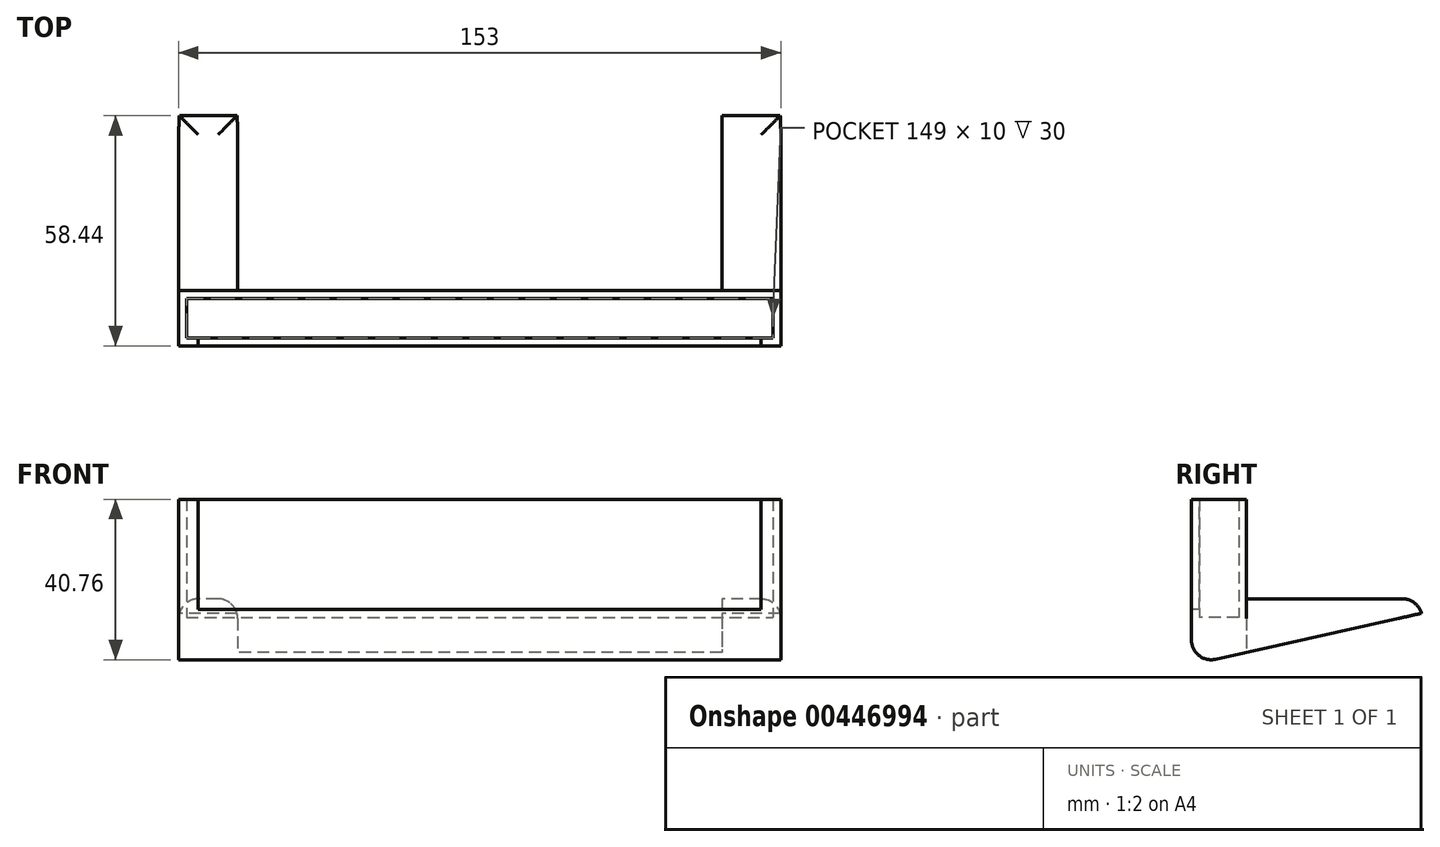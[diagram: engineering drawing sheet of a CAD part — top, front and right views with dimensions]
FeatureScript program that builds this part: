
annotation { "Feature Type Name" : "Feature", "Feature Type Description" : "" }
export const myFeature = defineFeature(function(context is Context, id is Id, definition is map)
    precondition{}
    {
        {
            var Q0;
            Q0=qCreatedBy(makeId("Top.planeOp"),FACE);
            var sketch = newSketch(context, id + "F0", { "sketchPlane" : qUnion([Q0])});
            skLineSegment(sketch, "E0.bottom", {"start": v(-58.19, 12) * mm, "end": v(90.81, 12) * mm});
            skLineSegment(sketch, "E0.top", {"start": v(-58.19, 2) * mm, "end": v(90.81, 2) * mm});
            skLineSegment(sketch, "E0.left", {"start": v(-58.19, 12) * mm, "end": v(-58.19, 2) * mm});
            skLineSegment(sketch, "E0.right", {"start": v(90.81, 12) * mm, "end": v(90.81, 2) * mm});
            skLineSegment(sketch, "E1.bottom", {"start": v(-60.19, 14) * mm, "end": v(92.81, 14) * mm});
            skLineSegment(sketch, "E1.top", {"start": v(-60.19, 0) * mm, "end": v(92.81, 0) * mm});
            skLineSegment(sketch, "E1.left", {"start": v(-60.19, 14) * mm, "end": v(-60.19, 0) * mm});
            skLineSegment(sketch, "E1.right", {"start": v(92.81, 14) * mm, "end": v(92.81, 0) * mm});
            skSolve(sketch);
        }
        {
            var Q0;
            Q0=makeQuery(id+"F0.imprint","IMPRINT",FACE,{"disambiguationData":[TD([[makeQuery(id+"F0.imprint","IMPRINT",EDGE,{"derivedFrom":sQuery(id+"F0.wireOp",EDGE,"E0.bottom")}),1.0]])]});
            extrude(context, id + "F1", {"entities" : qUnion([Q0]), "depth" : 32 * mm});
        }
        {
            var Q0;
            Q0=makeQuery(id+"F0.imprint","IMPRINT",FACE,{"disambiguationData":[TD([[makeQuery(id+"F0.imprint","IMPRINT",EDGE,{"derivedFrom":sQuery(id+"F0.wireOp",EDGE,"E0.bottom")}),-1.0]])]});
            extrude(context, id + "F2", {"entities" : qUnion([Q0]), "operationType" : NewBodyOperationType.ADD, "depth" : 2 * mm});
        }
        {
            var Q0;
            Q0=makeQuery(id+"F1.opExtrude","SWEPT_FACE",FACE,{"disambiguationData":[OSD([sQuery(id+"F0.wireOp",EDGE,"E1.top")])]});
            var sketch = newSketch(context, id + "F3", { "sketchPlane" : qUnion([Q0])});
            skLineSegment(sketch, "E2.bottom", {"start": v(-55.19, 32) * mm, "end": v(87.81, 32) * mm});
            skLineSegment(sketch, "E2.top", {"start": v(-55.19, 4) * mm, "end": v(87.81, 4) * mm});
            skLineSegment(sketch, "E2.left", {"start": v(-55.19, 32) * mm, "end": v(-55.19, 4) * mm});
            skLineSegment(sketch, "E2.right", {"start": v(87.81, 32) * mm, "end": v(87.81, 4) * mm});
            skSolve(sketch);
        }
        {
            var Q0;
            Q0=makeQuery(id+"F3.imprint","IMPRINT",FACE,{"disambiguationData":[TD([[makeQuery(id+"F3.imprint","IMPRINT",EDGE,{"derivedFrom":sQuery(id+"F3.wireOp",EDGE,"E2.bottom")}),-1.0]])]});
            extrude(context, id + "F4", {"entities" : qUnion([Q0]), "operationType" : NewBodyOperationType.REMOVE, "oppositeDirection" : true, "depth" : 5 * mm});
        }
        {
            var Q0;
            Q0 = qSketchRegion(id + "F0", true);
            var Q1;
            Q1=makeQuery(id+"F0.imprint","IMPRINT",FACE,{"disambiguationData":[TD([[makeQuery(id+"F0.imprint","IMPRINT",EDGE,{"derivedFrom":sQuery(id+"F0.wireOp",EDGE,"E0.bottom")}),-1.0]])]});
            extrude(context, id + "F5", {"entities" : qUnion([Q0, Q1]), "operationType" : NewBodyOperationType.ADD, "depth" : -10 * mm});
        }
        {
            var Q0;
            {var subQ0=sQuery(id+"F0.wireOp",EDGE,"E1.left");Q0=makeQuery(id+"F5.boolean.opBoolean","MERGE",FACE,{"derivedFrom":[makeQuery(id+"F1.opExtrude","SWEPT_FACE",FACE,{"disambiguationData":[OSD([subQ0])]}),makeQuery(id+"F5.opExtrude","SWEPT_FACE",FACE,{"disambiguationData":[OSD([subQ0])]})]});}
            var sketch = newSketch(context, id + "F6", { "sketchPlane" : qUnion([Q0])});
            skLineSegment(sketch, "E3", {"start": v(0, -10) * mm, "end": v(-58.44, 3.03) * mm});
            skLineSegment(sketch, "E4", {"start": v(-58.44, 3.03) * mm, "end": v(-58.44, 6.7) * mm});
            skLineSegment(sketch, "E5", {"start": v(-58.44, 6.7) * mm, "end": v(-14, 6.7) * mm});
            skLineSegment(sketch, "E6", {"start": v(-14, 6.7) * mm, "end": v(-14, -6.88) * mm});
            skLineSegment(sketch, "E7", {"start": v(0, -10) * mm, "end": v(-31.24, -10) * mm});
            skLineSegment(sketch, "E8", {"start": v(-31.24, -10) * mm, "end": v(-31.24, -3.03) * mm});
            skSolve(sketch);
        }
        {
            var Q0;
            {var subQ0=sQuery(id+"F6.wireOp",EDGE,"E7");var subQ1=sQuery(id+"F6.wireOp",EDGE,"E3");var subQ2=sQuery(id+"F0.wireOp",EDGE,"E1.left");var subQ3=sQuery(id+"F0.wireOp",EDGE,"E1.top");var subQ4=makeQuery(id+"F6.imprint","INTERSECT",VERTEX,{"derivedFrom":[makeQuery(id+"F5.boolean.opBoolean","MERGE",EDGE,{"derivedFrom":[makeQuery(id+"F1.opExtrude","SWEPT_EDGE",EDGE,{"disambiguationData":[OSD([subQ3,subQ2])]}),makeQuery(id+"F5.opExtrude","SWEPT_EDGE",EDGE,{"disambiguationData":[OSD([subQ3,subQ2])]})]}),subQ1,subQ0]});Q0=makeQuery(id+"F6.imprint","IMPRINT",FACE,{"disambiguationData":[TD([[makeQuery(id+"F6.imprint","IMPRINT",EDGE,{"disambiguationData":[TD([[subQ4,1.0]])],"derivedFrom":subQ0}),1.0]])]});}
            extrude(context, id + "F7", {"entities" : qUnion([Q0]), "operationType" : NewBodyOperationType.REMOVE, "oppositeDirection" : true, "depth" : 250 * mm});
        }
        {
            var Q0;
            {var subQ0=sQuery(id+"F6.wireOp",EDGE,"E4");Q0=makeQuery(id+"F6.imprint","IMPRINT",FACE,{"disambiguationData":[TD([[makeQuery(id+"F6.imprint","IMPRINT",EDGE,{"derivedFrom":subQ0}),-1.0]])]});}
            extrude(context, id + "F8", {"entities" : qUnion([Q0]), "operationType" : NewBodyOperationType.ADD, "depth" : -153 * mm});
        }
        {
            var Q0;
            {var subQ0=sQuery(id+"F0.wireOp",EDGE,"E1.bottom");Q0=makeQuery(id+"F5.boolean.opBoolean","MERGE",FACE,{"derivedFrom":[makeQuery(id+"F1.opExtrude","SWEPT_FACE",FACE,{"disambiguationData":[OSD([subQ0])]}),makeQuery(id+"F5.opExtrude","SWEPT_FACE",FACE,{"disambiguationData":[OSD([subQ0])]})]});}
            var sketch = newSketch(context, id + "F9", { "sketchPlane" : qUnion([Q0])});
            skLineSegment(sketch, "E9.bottom", {"start": v(-77.81, 22) * mm, "end": v(45.19, 22) * mm});
            skLineSegment(sketch, "E9.top", {"start": v(-77.81, -11.16) * mm, "end": v(45.19, -11.16) * mm});
            skLineSegment(sketch, "E9.left", {"start": v(-77.81, 22) * mm, "end": v(-77.81, -11.16) * mm});
            skLineSegment(sketch, "E9.right", {"start": v(45.19, 22) * mm, "end": v(45.19, -11.16) * mm});
            skSolve(sketch);
        }
        {
            var Q0;
            {var subQ0=sQuery(id+"F9.wireOp",EDGE,"E9.top");Q0=makeQuery(id+"F9.imprint","IMPRINT",FACE,{"disambiguationData":[TD([[makeQuery(id+"F9.imprint","IMPRINT",EDGE,{"derivedFrom":subQ0}),1.0]])]});}
            extrude(context, id + "F10", {"entities" : qUnion([Q0]), "operationType" : NewBodyOperationType.REMOVE, "oppositeDirection" : true, "depth" : -125 * mm});
        }
        {
            var Q0;
            Q0=makeQuery(id+"F10.boolean.opBoolean","COPY",EDGE,{"derivedFrom":makeQuery(id+"F10.opExtrude","SWEPT_EDGE",EDGE,{"disambiguationData":[OSD([sQuery(id+"F0.wireOp",EDGE,"E1.bottom"),sQuery(id+"F0.wireOp",EDGE,"E1.left"),sQuery(id+"F6.wireOp",EDGE,"E5"),sQuery(id+"F6.wireOp",EDGE,"E6"),sQuery(id+"F9.wireOp",EDGE,"E9.left")])]})});
            var Q1;
            Q1=makeQuery(id+"F8.opExtrude","CAP_EDGE",EDGE,{"disambiguationData":[OSD([sQuery(id+"F6.wireOp",EDGE,"E5")])],"isStart":false});
            var Q2;
            Q2=makeQuery(id+"F10.boolean.opBoolean","COPY",EDGE,{"derivedFrom":makeQuery(id+"F10.opExtrude","SWEPT_EDGE",EDGE,{"disambiguationData":[OSD([sQuery(id+"F0.wireOp",EDGE,"E1.bottom"),sQuery(id+"F0.wireOp",EDGE,"E1.left"),sQuery(id+"F6.wireOp",EDGE,"E5"),sQuery(id+"F6.wireOp",EDGE,"E6"),sQuery(id+"F9.wireOp",EDGE,"E9.right")])]})});
            var Q3;
            Q3=makeQuery(id+"F8.opExtrude","CAP_EDGE",EDGE,{"disambiguationData":[OSD([sQuery(id+"F6.wireOp",EDGE,"E5")])],"isStart":true});
            var Q4;
            {var subQ0=sQuery(id+"F6.wireOp",EDGE,"E4");var subQ1=sQuery(id+"F0.wireOp",EDGE,"E1.right");var subQ2=sQuery(id+"F6.wireOp",EDGE,"E5");Q4=makeQuery(id+"F10.boolean.opBoolean","SPLIT",EDGE,{"disambiguationData":[TD([makeQuery(id+"F1.opExtrude","SWEPT_FACE",FACE,{"disambiguationData":[OSD([subQ1])]})])],"derivedFrom":makeQuery(id+"F8.opExtrude","SWEPT_EDGE",EDGE,{"disambiguationData":[OSD([subQ0,subQ2])]})});}
            var Q5;
            {var subQ0=sQuery(id+"F6.wireOp",EDGE,"E5");var subQ1=sQuery(id+"F6.wireOp",EDGE,"E4");var subQ2=sQuery(id+"F0.wireOp",EDGE,"E1.left");Q5=makeQuery(id+"F10.boolean.opBoolean","SPLIT",EDGE,{"disambiguationData":[TD([makeQuery(id+"F1.opExtrude","SWEPT_FACE",FACE,{"disambiguationData":[OSD([subQ2])]})])],"derivedFrom":makeQuery(id+"F8.opExtrude","SWEPT_EDGE",EDGE,{"disambiguationData":[OSD([subQ1,subQ0])]})});}
            var Q6;
            {var subQ0=sQuery(id+"F0.wireOp",EDGE,"E1.top");Q6=makeQuery(id+"F7.boolean.opBoolean","MERGE",EDGE,{"derivedFrom":[makeQuery(id+"F5.opExtrude","CAP_EDGE",EDGE,{"disambiguationData":[OSD([subQ0])],"isStart":false}),makeQuery(id+"F7.opExtrude","SWEPT_EDGE",EDGE,{"disambiguationData":[OSD([subQ0,sQuery(id+"F0.wireOp",EDGE,"E1.left"),sQuery(id+"F6.wireOp",EDGE,"E3"),sQuery(id+"F6.wireOp",EDGE,"E7")])]})]});}
            fillet(context, id + "F11", {"entities" : qUnion([Q0, Q1, Q2, Q3, Q4, Q5, Q6]), "radius" : 5 * mm, "tangentPropagation" : true, "allowEdgeOverflow" : false});
        }
    });
